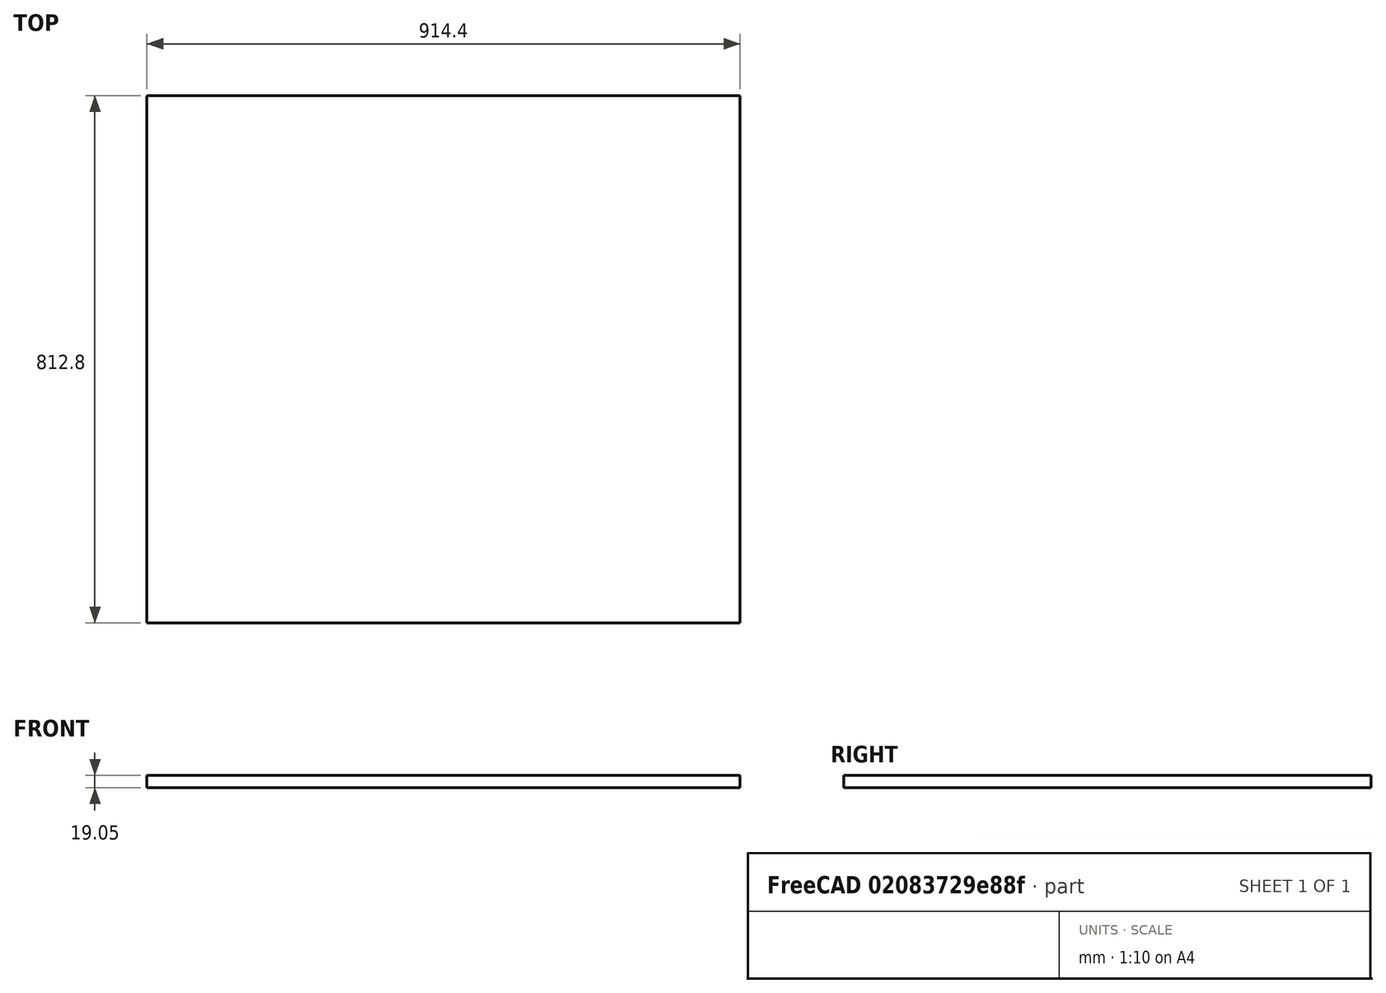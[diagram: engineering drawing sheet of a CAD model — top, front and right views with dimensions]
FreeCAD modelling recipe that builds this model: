
FCSTD DOCUMENT  (FreeCAD 0.19R)
Label: Side_Wall
License: Creative Commons Attribution
LicenseURL: http://creativecommons.org/licenses/by/4.0/
objects: Sketcher::SketchObject×1, Part::Extrusion×1
note: 2 computed .brp shape members not serialized (recipe doc carries the construction recipe); baked Part::Feature solids carry a one-line shape summary decoded from their .brp

FEATURE [Sketcher::SketchObject] Sketch001  label="Sketch_B"
  sketch-geometry (4):
    g0: LineSegment StartX=0 StartY=0 StartZ=0 EndX=914.4 EndY=0 EndZ=0
    g1: LineSegment StartX=914.4 StartY=0 StartZ=0 EndX=914.4 EndY=812.8 EndZ=0
    g2: LineSegment StartX=914.4 StartY=812.8 StartZ=0 EndX=0 EndY=812.8 EndZ=0
    g3: LineSegment StartX=0 StartY=812.8 StartZ=0 EndX=0 EndY=0 EndZ=0
  constraints (11):
    c: Coincident(g0,g1)
    c: Coincident(g1,g2)
    c: Coincident(g2,g3)
    c: Coincident(g3,g0)
    c: Horizontal(g0)
    c: Horizontal(g2)
    c: Vertical(g1)
    c: Vertical(g3)
    c: Distance(g0) = 914.4
    c: Distance(g1) = 812.8
    c: Coincident(g-1,g0)
FEATURE [Part::Extrusion] Extrude001  label="Part_B_Side_Wall_001"
  Base = -> Sketch001
  Dir = (0,0,1)
  DirMode = 2
  FaceMakerClass = Part::FaceMakerBullseye
  LengthFwd = 19.05
  LengthRev = 0
  Placement = pos=(8.1e-14,7.6e-14,0) rot=(0,0,1;0rad)
  Solid = true
  Symmetric = false
